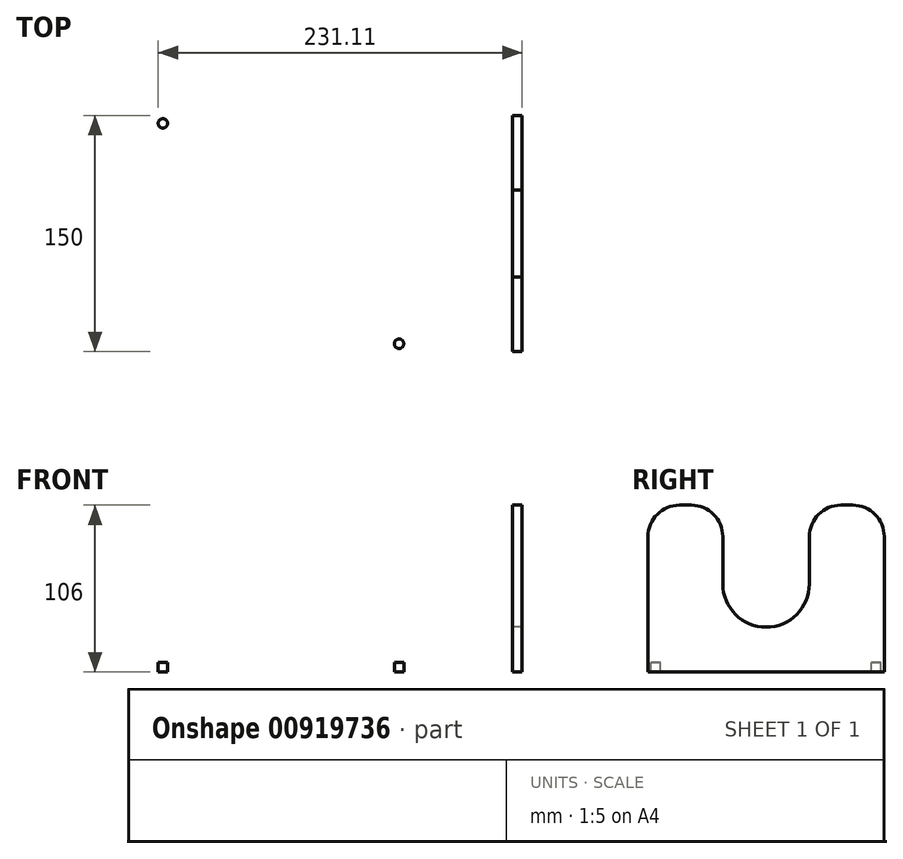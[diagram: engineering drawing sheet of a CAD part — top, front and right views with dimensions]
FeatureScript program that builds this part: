
annotation { "Feature Type Name" : "Feature", "Feature Type Description" : "" }
export const myFeature = defineFeature(function(context is Context, id is Id, definition is map)
    precondition{}
    {
        {
            var Q0;
            Q0=qCreatedBy(makeId("Top.planeOp"),FACE);
            var sketch = newSketch(context, id + "F0", { "sketchPlane" : qUnion([Q0])});
            skCircle(sketch, "E0", {"center": v(0, 0) * mm, "radius": 3.5 * mm});
            skLineSegment(sketch, "E1", {"start": v(0, 0) * mm, "end": v(-3.5, 0) * mm, "construction": true});
            skLineSegment(sketch, "E2", {"start": v(-3.5, 0) * mm, "end": v(-8.5, 0) * mm, "construction": true});
            skLineSegment(sketch, "E3", {"start": v(-8.5, 0) * mm, "end": v(-8.5, -17.5) * mm});
            skLineSegment(sketch, "E4", {"start": v(-8.5, 0) * mm, "end": v(-8.5, 17.5) * mm});
            skLineSegment(sketch, "E5", {"start": v(11.5, 37.5) * mm, "end": v(41.5, 37.5) * mm});
            skLineSegment(sketch, "E6", {"start": v(41.5, 37.5) * mm, "end": v(73.14, 69.14) * mm});
            skLineSegment(sketch, "E7", {"start": v(87.28, 75) * mm, "end": v(381.5, 75) * mm});
            skLineSegment(sketch, "E8.MirrorCS", {"start": v(11.5, -37.5) * mm, "end": v(41.5, -37.5) * mm});
            skLineSegment(sketch, "E9.MirrorCS", {"start": v(41.5, -37.5) * mm, "end": v(73.14, -69.14) * mm});
            skLineSegment(sketch, "E10.MirrorCS", {"start": v(87.28, -75) * mm, "end": v(381.5, -75) * mm});
            skLineSegment(sketch, "E11", {"start": v(381.5, 75) * mm, "end": v(381.5, -75) * mm});
            skLineSegment(sketch, "E12.0", {"start": v(387.5, 75) * mm, "end": v(387.5, -75) * mm});
            skLineSegment(sketch, "E13", {"start": v(387.5, -75) * mm, "end": v(381.5, -75) * mm});
            skLineSegment(sketch, "E14", {"start": v(387.5, 75) * mm, "end": v(381.5, 75) * mm});
            skPoint(sketch, "E15.visualSharp", {"position": v(-8.5, 37.5) * mm});
            skArc(sketch, "E15.filletArc", {"start": v(11.5, 37.5) * mm, "mid": v(-2.64, 31.64) * mm, "end": v(-8.5, 17.5) * mm});
            skPoint(sketch, "E16.visualSharp", {"position": v(-8.5, -37.5) * mm});
            skArc(sketch, "E16.filletArc", {"start": v(-8.5, -17.5) * mm, "mid": v(-2.64, -31.64) * mm, "end": v(11.5, -37.5) * mm});
            skPoint(sketch, "E17.visualSharp", {"position": v(79, -75) * mm});
            skArc(sketch, "E17.filletArc", {"start": v(73.14, -69.14) * mm, "mid": v(79.63, -73.48) * mm, "end": v(87.28, -75) * mm});
            skPoint(sketch, "E18.visualSharp", {"position": v(79, 75) * mm});
            skArc(sketch, "E18.filletArc", {"start": v(87.28, 75) * mm, "mid": v(79.63, 73.48) * mm, "end": v(73.14, 69.14) * mm});
            skSolve(sketch);
        }
        {
            var Q0;
            Q0=makeQuery(id+"F0.imprint","IMPRINT",FACE,{"disambiguationData":[TD([[makeQuery(id+"F0.imprint","IMPRINT",EDGE,{"derivedFrom":sQuery(id+"F0.wireOp",EDGE,"E0")}),-1.0]])]});
            extrude(context, id + "F1", {"entities" : qUnion([Q0]), "endBound" : BoundingType.SYMMETRIC, "depth" : 6 * mm, "offsetDistance" : 25 * mm});
        }
        {
            var Q0;
            Q0=makeQuery(id+"F0.imprint","IMPRINT",FACE,{"disambiguationData":[TD([[makeQuery(id+"F0.imprint","IMPRINT",EDGE,{"derivedFrom":sQuery(id+"F0.wireOp",EDGE,"E11")}),1.0]])]});
            var Q1;
            Q1=makeQuery(id+"F1.opExtrude","CAP_FACE",FACE,{"disambiguationData":[OSD([sQuery(id+"F0.wireOp",EDGE,"E0"),sQuery(id+"F0.wireOp",EDGE,"E3"),sQuery(id+"F0.wireOp",EDGE,"E4"),sQuery(id+"F0.wireOp",EDGE,"E5"),sQuery(id+"F0.wireOp",EDGE,"E6"),sQuery(id+"F0.wireOp",EDGE,"E7"),sQuery(id+"F0.wireOp",EDGE,"E8.MirrorCS"),sQuery(id+"F0.wireOp",EDGE,"E9.MirrorCS"),sQuery(id+"F0.wireOp",EDGE,"E10.MirrorCS"),sQuery(id+"F0.wireOp",EDGE,"E11")])],"isStart":true});
            extrude(context, id + "F2", {"entities" : qUnion([Q0]), "operationType" : NewBodyOperationType.ADD, "depth" : 103 * mm, "offsetDistance" : 25 * mm, "hasSecondDirection" : true, "secondDirectionBound" : SecondDirectionBoundingType.UP_TO_SURFACE, "secondDirectionOppositeDirection" : true, "secondDirectionDepth" : 25 * mm, "secondDirectionBoundEntityFace" : qUnion([Q1])});
        }
        {
            var Q0;
            Q0=makeQuery(id+"F2.opExtrude","SWEPT_FACE",FACE,{"disambiguationData":[OSD([sQuery(id+"F0.wireOp",EDGE,"E11")])]});
            var sketch = newSketch(context, id + "F3", { "sketchPlane" : qUnion([Q0])});
            skLineSegment(sketch, "E19.0.0", {"start": v(-75, 83) * mm, "end": v(-75, 3) * mm});
            skLineSegment(sketch, "E19.0.1", {"start": v(-75, 3) * mm, "end": v(75, 3) * mm});
            skLineSegment(sketch, "E19.0.2", {"start": v(75, 3) * mm, "end": v(75, 83) * mm});
            skLineSegment(sketch, "E19.0.3", {"start": v(55, 103) * mm, "end": v(47.5, 103) * mm});
            skLineSegment(sketch, "E20", {"start": v(75, 3) * mm, "end": v(-75, 103) * mm, "construction": true});
            skCircle(sketch, "E21", {"center": v(0, 53) * mm, "radius": 27.5 * mm});
            skPoint(sketch, "E22.visualSharp", {"position": v(75, 103) * mm});
            skArc(sketch, "E22.filletArc", {"start": v(75, 83) * mm, "mid": v(69.14, 97.14) * mm, "end": v(55, 103) * mm});
            skPoint(sketch, "E23.visualSharp", {"position": v(-75, 103) * mm});
            skArc(sketch, "E23.filletArc", {"start": v(-55, 103) * mm, "mid": v(-69.14, 97.14) * mm, "end": v(-75, 83) * mm});
            skLineSegment(sketch, "E24", {"start": v(-75, 83) * mm, "end": v(-75, 103) * mm});
            skLineSegment(sketch, "E25", {"start": v(-55, 103) * mm, "end": v(-75, 103) * mm});
            skLineSegment(sketch, "E26", {"start": v(75, 103) * mm, "end": v(55, 103) * mm});
            skLineSegment(sketch, "E27", {"start": v(75, 103) * mm, "end": v(75, 83) * mm});
            skLineSegment(sketch, "E28", {"start": v(0, 53) * mm, "end": v(-27.5, 53) * mm, "construction": true});
            skLineSegment(sketch, "E29", {"start": v(0, 53) * mm, "end": v(27.5, 53) * mm, "construction": true});
            skLineSegment(sketch, "E30", {"start": v(27.5, 53) * mm, "end": v(27.5, 83) * mm});
            skLineSegment(sketch, "E31", {"start": v(-27.5, 53) * mm, "end": v(-27.5, 83) * mm});
            skLineSegment(sketch, "E32", {"start": v(-27.5, 103) * mm, "end": v(32.5, 103) * mm});
            skPoint(sketch, "E33.newPointA", {"position": v(27.5, 103) * mm});
            skArc(sketch, "E33.filletArc", {"start": v(47.5, 103) * mm, "mid": v(33.36, 97.14) * mm, "end": v(27.5, 83) * mm});
            skLineSegment(sketch, "E34", {"start": v(-55, 103) * mm, "end": v(-47.5, 103) * mm});
            skPoint(sketch, "E35.visualSharp", {"position": v(-27.5, 103) * mm});
            skArc(sketch, "E35.filletArc", {"start": v(-27.5, 83) * mm, "mid": v(-33.36, 97.14) * mm, "end": v(-47.5, 103) * mm});
            skSolve(sketch);
        }
        {
            var Q0;
            Q0=makeQuery(id+"F3.imprint","IMPRINT",FACE,{"disambiguationData":[TD([[makeQuery(id+"F3.imprint","IMPRINT",EDGE,{"derivedFrom":sQuery(id+"F3.wireOp",EDGE,"E21")}),1.0]])]});
            var Q1;
            Q1=makeQuery(id+"F3.imprint","IMPRINT",FACE,{"disambiguationData":[TD([[makeQuery(id+"F3.imprint","IMPRINT",EDGE,{"derivedFrom":sQuery(id+"F3.wireOp",EDGE,"E22.filletArc")}),-1.0]])]});
            var Q2;
            Q2=makeQuery(id+"F3.imprint","IMPRINT",FACE,{"disambiguationData":[TD([[makeQuery(id+"F3.imprint","IMPRINT",EDGE,{"derivedFrom":sQuery(id+"F3.wireOp",EDGE,"E23.filletArc")}),-1.0]])]});
            var Q3;
            {var subQ0=sQuery(id+"F3.wireOp",EDGE,"E30");Q3=makeQuery(id+"F3.imprint","IMPRINT",FACE,{"disambiguationData":[TD([[makeQuery(id+"F3.imprint","IMPRINT",EDGE,{"derivedFrom":subQ0}),1.0]])]});}
            extrude(context, id + "F4", {"entities" : qUnion([Q0, Q1, Q2, Q3]), "operationType" : NewBodyOperationType.REMOVE, "oppositeDirection" : true, "depth" : 25 * mm, "offsetDistance" : 25 * mm});
        }
        {
            var Q0;
            Q0=makeQuery(id+"F1.opExtrude","CAP_FACE",FACE,{"disambiguationData":[OSD([sQuery(id+"F0.wireOp",EDGE,"E0"),sQuery(id+"F0.wireOp",EDGE,"E3"),sQuery(id+"F0.wireOp",EDGE,"E4"),sQuery(id+"F0.wireOp",EDGE,"E5"),sQuery(id+"F0.wireOp",EDGE,"E6"),sQuery(id+"F0.wireOp",EDGE,"E7"),sQuery(id+"F0.wireOp",EDGE,"E8.MirrorCS"),sQuery(id+"F0.wireOp",EDGE,"E9.MirrorCS"),sQuery(id+"F0.wireOp",EDGE,"E10.MirrorCS"),sQuery(id+"F0.wireOp",EDGE,"E11"),sQuery(id+"F0.wireOp",EDGE,"E15.filletArc"),sQuery(id+"F0.wireOp",EDGE,"E16.filletArc"),sQuery(id+"F0.wireOp",EDGE,"E17.filletArc"),sQuery(id+"F0.wireOp",EDGE,"E18.filletArc")])],"isStart":false});
            var sketch = newSketch(context, id + "F5", { "sketchPlane" : qUnion([Q0])});
            skLineSegment(sketch, "E36.0", {"start": v(87.28, -75) * mm, "end": v(381.5, -75) * mm, "construction": true});
            skLineSegment(sketch, "E37.0", {"start": v(87.28, 75) * mm, "end": v(381.5, 75) * mm, "construction": true});
            skLineSegment(sketch, "E38", {"start": v(234.4, -75) * mm, "end": v(234.4, 75) * mm});
            skLineSegment(sketch, "E39", {"start": v(234.4, 0) * mm, "end": v(159.4, 0) * mm, "construction": true});
            skLineSegment(sketch, "E40", {"start": v(234.4, 0) * mm, "end": v(309.4, 0) * mm, "construction": true});
            skLineSegment(sketch, "E41", {"start": v(309.4, 0) * mm, "end": v(309.4, 70) * mm, "construction": true});
            skLineSegment(sketch, "E42", {"start": v(309.4, 0) * mm, "end": v(309.4, -70) * mm, "construction": true});
            skCircle(sketch, "E43", {"center": v(309.4, 70) * mm, "radius": 3 * mm});
            skCircle(sketch, "E44.MirrorC", {"center": v(309.4, -70) * mm, "radius": 3 * mm});
            skCircle(sketch, "E45.MirrorC", {"center": v(159.4, 70) * mm, "radius": 3 * mm});
            skCircle(sketch, "E46.MirrorC", {"center": v(159.4, -70) * mm, "radius": 3 * mm});
            skSolve(sketch);
        }
        {
            var Q0;
            Q0=makeQuery(id+"F5.imprint","IMPRINT",FACE,{"disambiguationData":[TD([[makeQuery(id+"F5.imprint","IMPRINT",EDGE,{"derivedFrom":sQuery(id+"F5.wireOp",EDGE,"E45.MirrorC")}),-1.0]])]});
            var Q1;
            Q1=makeQuery(id+"F5.imprint","IMPRINT",FACE,{"disambiguationData":[TD([[makeQuery(id+"F5.imprint","IMPRINT",EDGE,{"derivedFrom":sQuery(id+"F5.wireOp",EDGE,"E43")}),1.0]])]});
            var Q2;
            Q2=makeQuery(id+"F5.imprint","IMPRINT",FACE,{"disambiguationData":[TD([[makeQuery(id+"F5.imprint","IMPRINT",EDGE,{"derivedFrom":sQuery(id+"F5.wireOp",EDGE,"E44.MirrorC")}),-1.0]])]});
            var Q3;
            Q3=makeQuery(id+"F5.imprint","IMPRINT",FACE,{"disambiguationData":[TD([[makeQuery(id+"F5.imprint","IMPRINT",EDGE,{"derivedFrom":sQuery(id+"F5.wireOp",EDGE,"E46.MirrorC")}),1.0]])]});
            extrude(context, id + "F6", {"entities" : qUnion([Q0, Q1, Q2, Q3]), "operationType" : NewBodyOperationType.REMOVE, "oppositeDirection" : true, "depth" : 25 * mm, "offsetDistance" : 25 * mm});
        }
    });
